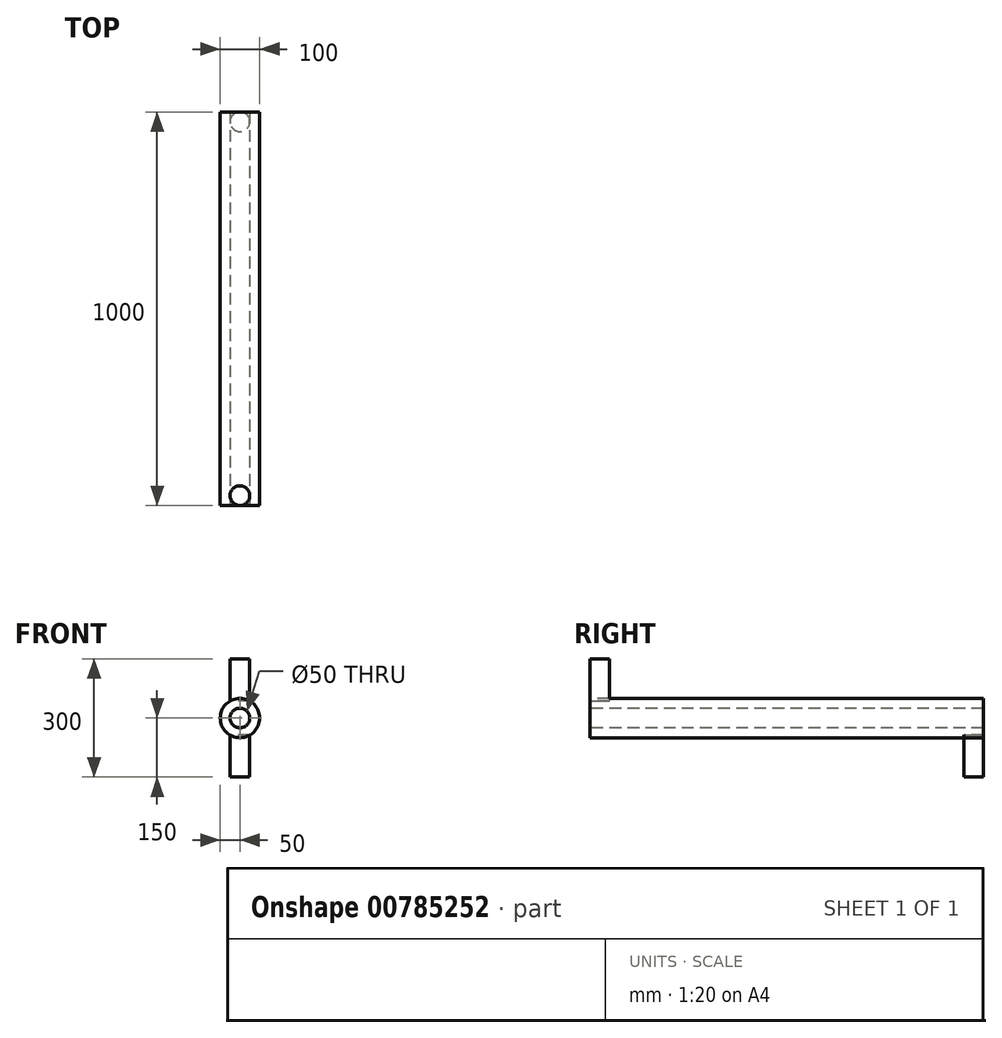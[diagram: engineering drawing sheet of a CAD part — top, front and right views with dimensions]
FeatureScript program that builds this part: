
annotation { "Feature Type Name" : "Feature", "Feature Type Description" : "" }
export const myFeature = defineFeature(function(context is Context, id is Id, definition is map)
    precondition{}
    {
        {
            var Q0;
            Q0=qCreatedBy(makeId("Front.planeOp"),FACE);
            var sketch = newSketch(context, id + "F0", { "sketchPlane" : qUnion([Q0])});
            skCircle(sketch, "E0", {"center": v(0, 0) * mm, "radius": 50 * mm});
            skCircle(sketch, "E1", {"center": v(0, 0) * mm, "radius": 25 * mm});
            skSolve(sketch);
        }
        {
            var Q0;
            Q0=makeQuery(id+"F0.imprint","IMPRINT",FACE,{"disambiguationData":[TD([[makeQuery(id+"F0.imprint","IMPRINT",EDGE,{"derivedFrom":sQuery(id+"F0.wireOp",EDGE,"E0")}),1.0]])]});
            var Q1;
            Q1=sQuery(id+"F0.wireOp",EDGE,"E0");
            extrude(context, id + "F1", {"entities" : qUnion([Q0]), "surfaceEntities" : qUnion([Q1]), "oppositeDirection" : true, "depth" : 1000 * mm, "offsetDistance" : 25 * mm});
        }
        {
            var Q0;
            Q0=qCreatedBy(makeId("Top.planeOp"),FACE);
            cPlane(context, id + "F2", {"entities" : qUnion([Q0]), "cplaneType" : CPlaneType.OFFSET, "offset" : 50 * mm, "width" : 150 * mm, "height" : 150 * mm});
        }
        {
            var Q0;
            Q0=qCreatedBy(id+"F2.planeOp",FACE);
            var sketch = newSketch(context, id + "F3", { "sketchPlane" : qUnion([Q0])});
            skCircle(sketch, "E2", {"center": v(0, 25) * mm, "radius": 25 * mm});
            skSolve(sketch);
        }
        {
            var Q0;
            Q0=qCreatedBy(makeId("Top.planeOp"),FACE);
            cPlane(context, id + "F4", {"entities" : qUnion([Q0]), "cplaneType" : CPlaneType.OFFSET, "offset" : 50 * mm, "oppositeDirection" : true, "width" : 150 * mm, "height" : 150 * mm});
        }
        {
            var Q0;
            Q0=qCreatedBy(id+"F4.planeOp",FACE);
            var sketch = newSketch(context, id + "F5", { "sketchPlane" : qUnion([Q0])});
            skCircle(sketch, "E3", {"center": v(0, 975) * mm, "radius": 25 * mm});
            skSolve(sketch);
        }
        {
            var Q0;
            Q0=makeQuery(id+"F5.imprint","IMPRINT",FACE,{"disambiguationData":[TD([[makeQuery(id+"F5.imprint","IMPRINT",EDGE,{"derivedFrom":sQuery(id+"F5.wireOp",EDGE,"E3")}),1.0]])]});
            extrude(context, id + "F6", {"entities" : qUnion([Q0]), "oppositeDirection" : true, "depth" : 100 * mm, "offsetDistance" : 25 * mm, "hasSecondDirection" : true, "secondDirectionOppositeDirection" : false, "secondDirectionDepth" : 7 * mm});
        }
        {
            var Q0;
            Q0 = qSketchRegion(id + "F3", true);
            var Q1;
            Q1=sQuery(id+"F3.wireOp",EDGE,"E2");
            extrude(context, id + "F7", {"entities" : qUnion([Q0]), "surfaceEntities" : qUnion([Q1]), "oppositeDirection" : true, "depth" : 7 * mm, "offsetDistance" : 25 * mm, "hasSecondDirection" : true, "secondDirectionOppositeDirection" : false, "secondDirectionDepth" : 100 * mm});
        }
    });
